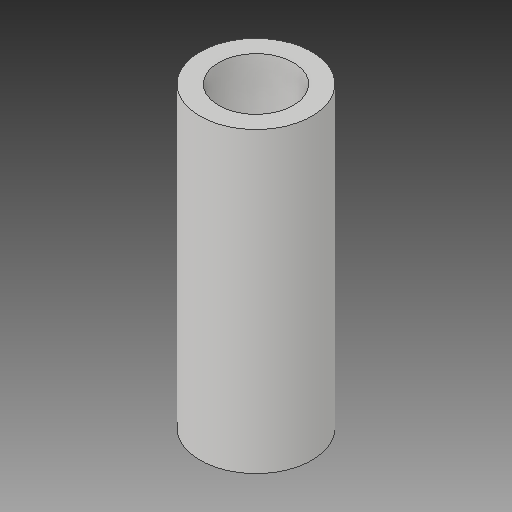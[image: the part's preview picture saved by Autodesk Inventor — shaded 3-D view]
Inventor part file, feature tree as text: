
AUTODESK INVENTOR PART (.ipt)
format: ipt  version: 2017 (Build 210142000, 142)  size: 94,720 bytes
history: native  units: in
note: dims shown in document units (in); Inventor stores cm internally (conversion verified against a paired STEP export)
features: extrude x1, sketch x1
ambient origin geometry x8: Origin, YZ Plane, XZ Plane, XY Plane, X Axis, Y Axis, Z Axis, Center Point
bodies: Solid1 (feature_tree)
feature tree (2):
  extrude  "Extrusion1"  Depth=2.0in
  sketch  "Sketch1"  dims[d0=0.75in d1=0.5in d2=2.0in d3=0.0in]
